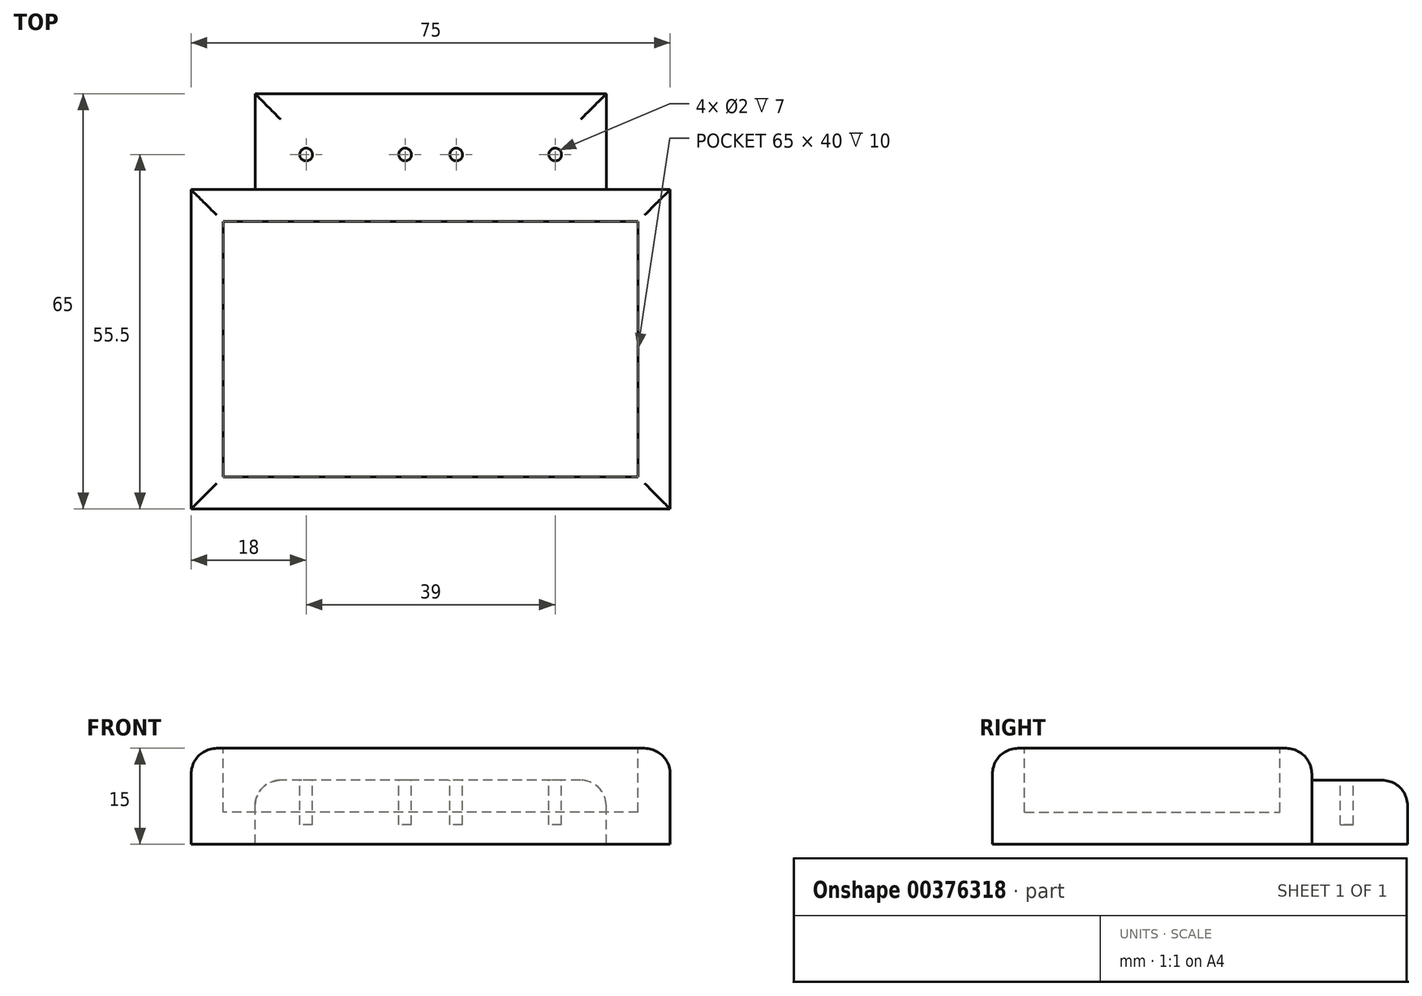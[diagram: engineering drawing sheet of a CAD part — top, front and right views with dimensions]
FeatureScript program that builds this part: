
annotation { "Feature Type Name" : "Feature", "Feature Type Description" : "" }
export const myFeature = defineFeature(function(context is Context, id is Id, definition is map)
    precondition{}
    {
        {
            var Q0;
            Q0=qCreatedBy(makeId("Top.planeOp"),FACE);
            var sketch = newSketch(context, id + "F0", { "sketchPlane" : qUnion([Q0])});
            skLineSegment(sketch, "E0.bottom", {"start": v(37.5, 25) * mm, "end": v(-37.5, 25) * mm});
            skLineSegment(sketch, "E0.top", {"start": v(37.5, -25) * mm, "end": v(-37.5, -25) * mm});
            skLineSegment(sketch, "E0.left", {"start": v(37.5, 25) * mm, "end": v(37.5, -25) * mm});
            skLineSegment(sketch, "E0.right", {"start": v(-37.5, 25) * mm, "end": v(-37.5, -25) * mm});
            skSolve(sketch);
        }
        {
            var Q0;
            Q0 = qSketchRegion(id + "F0", true);
            extrude(context, id + "F1", {"entities" : qUnion([Q0]), "depth" : 5 * mm});
        }
        {
            var Q0;
            Q0=makeQuery(id+"F1.opExtrude","CAP_FACE",FACE,{"disambiguationData":[OSD([sQuery(id+"F0.wireOp",EDGE,"hRz4pzWG-V5UF-O48R-vMyP-0FwJZYAUdx2B.bottom"),sQuery(id+"F0.wireOp",EDGE,"hRz4pzWG-V5UF-O48R-vMyP-0FwJZYAUdx2B.top"),sQuery(id+"F0.wireOp",EDGE,"hRz4pzWG-V5UF-O48R-vMyP-0FwJZYAUdx2B.left"),sQuery(id+"F0.wireOp",EDGE,"hRz4pzWG-V5UF-O48R-vMyP-0FwJZYAUdx2B.right"),sQuery(id+"F0.wireOp",EDGE,"E0.bottom"),sQuery(id+"F0.wireOp",EDGE,"E0.top"),sQuery(id+"F0.wireOp",EDGE,"E0.left"),sQuery(id+"F0.wireOp",EDGE,"E0.right")])],"isStart":true});
            var sketch = newSketch(context, id + "F2", { "sketchPlane" : qUnion([Q0])});
            skLineSegment(sketch, "E1.bottom", {"start": v(-37.5, 25) * mm, "end": v(37.5, 25) * mm});
            skLineSegment(sketch, "E1.left", {"start": v(-37.5, 25) * mm, "end": v(-37.5, -25) * mm});
            skLineSegment(sketch, "E1.right", {"start": v(37.5, 25) * mm, "end": v(37.5, -25) * mm});
            skLineSegment(sketch, "E2", {"start": v(-37.5, -25) * mm, "end": v(-27.5, -25) * mm});
            skLineSegment(sketch, "E3", {"start": v(-27.5, -25) * mm, "end": v(-27.5, -40) * mm});
            skLineSegment(sketch, "E4", {"start": v(-27.5, -40) * mm, "end": v(27.5, -40) * mm});
            skLineSegment(sketch, "E5", {"start": v(27.5, -40) * mm, "end": v(27.5, -25) * mm});
            skLineSegment(sketch, "E6", {"start": v(27.5, -25) * mm, "end": v(37.5, -25) * mm});
            skSolve(sketch);
        }
        {
            var Q0;
            Q0 = qSketchRegion(id + "F2", true);
            extrude(context, id + "F3", {"entities" : qUnion([Q0]), "operationType" : NewBodyOperationType.ADD, "depth" : 10 * mm});
        }
        {
            var Q0;
            Q0=makeQuery(id+"F1.opExtrude","CAP_EDGE",EDGE,{"disambiguationData":[OSD([sQuery(id+"F0.wireOp",EDGE,"E0.top")])],"isStart":false});
            var Q1;
            Q1=makeQuery(id+"F1.opExtrude","CAP_EDGE",EDGE,{"disambiguationData":[OSD([sQuery(id+"F0.wireOp",EDGE,"E0.left")])],"isStart":false});
            var Q2;
            Q2=makeQuery(id+"F1.opExtrude","CAP_EDGE",EDGE,{"disambiguationData":[OSD([sQuery(id+"F0.wireOp",EDGE,"E0.bottom")])],"isStart":false});
            var Q3;
            Q3=makeQuery(id+"F1.opExtrude","CAP_EDGE",EDGE,{"disambiguationData":[OSD([sQuery(id+"F0.wireOp",EDGE,"E0.right")])],"isStart":false});
            var Q4;
            Q4=makeQuery(id+"F3.opExtrude","CAP_EDGE",EDGE,{"disambiguationData":[OSD([sQuery(id+"F2.wireOp",EDGE,"E5")])],"isStart":true});
            var Q5;
            Q5=makeQuery(id+"F3.opExtrude","CAP_EDGE",EDGE,{"disambiguationData":[OSD([sQuery(id+"F2.wireOp",EDGE,"E4")])],"isStart":true});
            var Q6;
            Q6=makeQuery(id+"F3.opExtrude","CAP_EDGE",EDGE,{"disambiguationData":[OSD([sQuery(id+"F2.wireOp",EDGE,"E3")])],"isStart":true});
            fillet(context, id + "F4", {"entities" : qUnion([Q0, Q1, Q2, Q3, Q4, Q5, Q6]), "radius" : 4 * mm, "tangentPropagation" : true, "allowEdgeOverflow" : false});
        }
        {
            var Q0;
            {var subQ0=sQuery(id+"F2.wireOp",EDGE,"E4");var subQ1=sQuery(id+"F2.wireOp",EDGE,"E3");var subQ2=sQuery(id+"F2.wireOp",EDGE,"E2");var subQ3=sQuery(id+"F2.wireOp",EDGE,"E5");var subQ4=sQuery(id+"F2.wireOp",EDGE,"E6");Q0=makeQuery(id+"F3.boolean.opBoolean","SPLIT",FACE,{"disambiguationData":[TD([makeQuery(id+"F1.opExtrude","SWEPT_FACE",FACE,{"disambiguationData":[OSD([sQuery(id+"F0.wireOp",EDGE,"E0.bottom")])]})])],"derivedFrom":makeQuery(id+"F3.opExtrude","CAP_FACE",FACE,{"disambiguationData":[OSD([sQuery(id+"F2.wireOp",EDGE,"E1.bottom"),sQuery(id+"F2.wireOp",EDGE,"E1.left"),sQuery(id+"F2.wireOp",EDGE,"E1.right"),subQ2,subQ1,subQ0,subQ3,subQ4])],"isStart":true})});}
            var sketch = newSketch(context, id + "F5", { "sketchPlane" : qUnion([Q0])});
            skCircle(sketch, "E7", {"center": v(-19.5, 30.5) * mm, "radius": 1 * mm});
            skPoint(sketch, "E7.centerSnap0", {"position": v(-23.5, 30.5) * mm});
            skCircle(sketch, "E8", {"center": v(-4, 30.5) * mm, "radius": 1 * mm});
            skCircle(sketch, "E9", {"center": v(4, 30.5) * mm, "radius": 1 * mm});
            skCircle(sketch, "E10", {"center": v(19.5, 30.5) * mm, "radius": 1 * mm});
            skSolve(sketch);
        }
        {
            var Q0;
            Q0 = qSketchRegion(id + "F5", true);
            extrude(context, id + "F6", {"entities" : qUnion([Q0]), "operationType" : NewBodyOperationType.REMOVE, "oppositeDirection" : true, "depth" : 7 * mm});
        }
        {
            var Q0;
            Q0=makeQuery(id+"F1.opExtrude","CAP_FACE",FACE,{"disambiguationData":[OSD([sQuery(id+"F0.wireOp",EDGE,"E0.bottom"),sQuery(id+"F0.wireOp",EDGE,"E0.top"),sQuery(id+"F0.wireOp",EDGE,"E0.left"),sQuery(id+"F0.wireOp",EDGE,"E0.right")])],"isStart":false});
            var sketch = newSketch(context, id + "F7", { "sketchPlane" : qUnion([Q0])});
            skLineSegment(sketch, "E11.bottom", {"start": v(32.5, -20) * mm, "end": v(-32.5, -20) * mm});
            skLineSegment(sketch, "E11.top", {"start": v(32.5, 20) * mm, "end": v(-32.5, 20) * mm});
            skLineSegment(sketch, "E11.left", {"start": v(32.5, -20) * mm, "end": v(32.5, 20) * mm});
            skLineSegment(sketch, "E11.right", {"start": v(-32.5, -20) * mm, "end": v(-32.5, 20) * mm});
            skPoint(sketch, "E11.middle", {"position": v(0, 0) * mm});
            skSolve(sketch);
        }
        {
            var Q0;
            Q0 = qSketchRegion(id + "F7", true);
            extrude(context, id + "F8", {"entities" : qUnion([Q0]), "operationType" : NewBodyOperationType.REMOVE, "oppositeDirection" : true, "depth" : 10 * mm});
        }
    });
